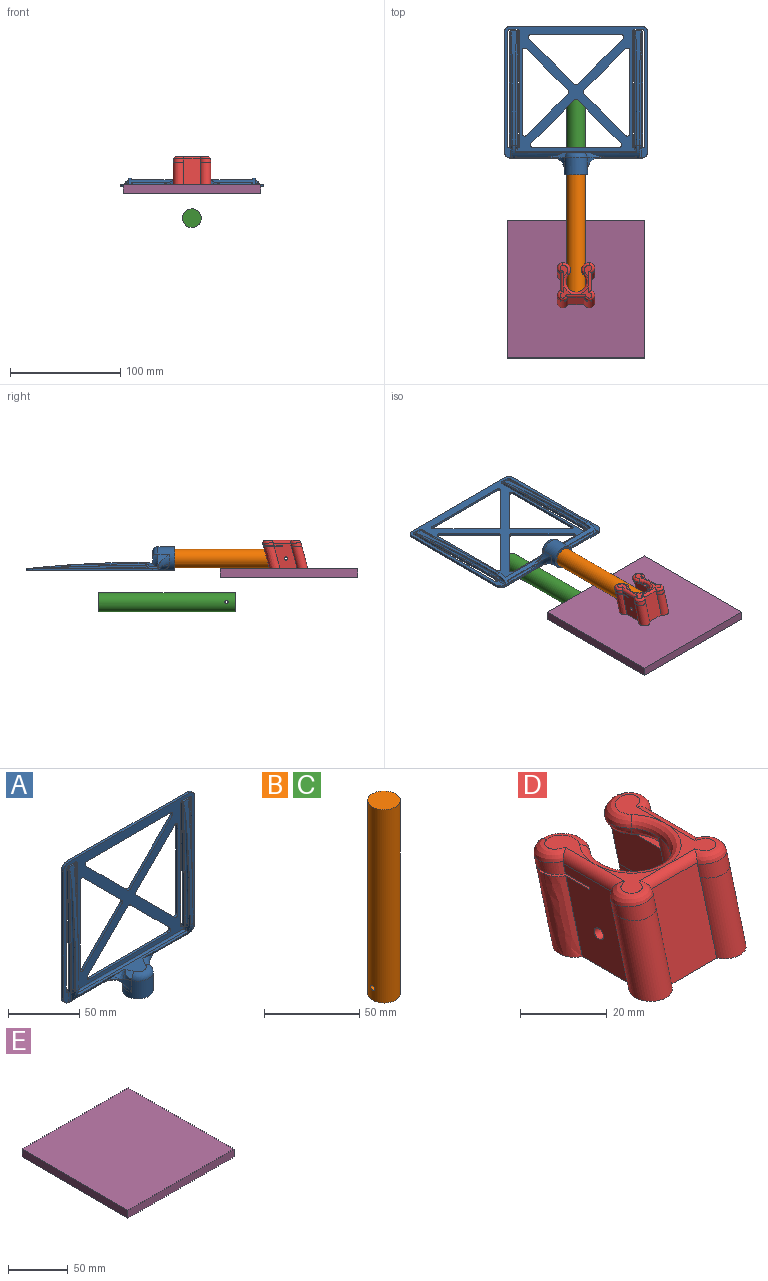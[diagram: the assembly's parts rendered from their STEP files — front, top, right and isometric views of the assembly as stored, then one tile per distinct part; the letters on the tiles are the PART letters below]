
ASSEMBLY  parts=5 mates=3
PART A: 120 faces, bbox 131.6x28.9x138.7 mm
  f0: plane 41.75x4.12mm, normal (0,0,-1), area 89.4mm2, adj f3,f11,f19,f53,f109,f115
  f1: plane 35.86x0.49mm, normal (0,0,-1), area 17.4mm2, adj f4,f9,f19,f113
  f2: cylinder r=15.3mm len=49.77mm, axis (-1,0,0), area 182.8mm2, adj f5,f7,f8,f14,f15,f17,f20,f101
  f3: plane 24.89x0.51mm, normal (0,-1,0), area 12.3mm2, adj f0,f4,f104,f109,f113
  f4: cylinder r=1.5mm len=34.86mm, axis (1,0,0), area 71.8mm2, adj f1,f3,f104,f113
  f5: plane 83.74x4mm, normal (-1,0,0), area 95.1mm2, adj f2,f20,f101,f102,f103
  f6: plane 83.74x4mm, normal (1,0,0), area 95.1mm2, adj f19,f21,f91,f92,f93
  f7: plane 80.18x4mm, normal (1,0,0), area 90.3mm2, adj f2,f17,f20,f94,f95,f96
  f8: plane 0.57x0.49mm, normal (1,0,0), area 0.1mm2, adj f2,f15,f106
  f9: plane 0.57x0.49mm, normal (-1,0,0), area 0.1mm2, adj f1,f19,f104
  f10: plane 80.18x4mm, normal (-1,0,0), area 90.3mm2, adj f17,f19,f21,f98,f99,f100
  f11: plane 131.62x121.62mm, normal (0,1,0), area 5467.3mm2, adj f0,f14,f24,f26,f36,f37,f38,f39
  f12: plane 6.61x0.05mm, normal (0,1,0), area 0.3mm2, adj f16,f27,f32,f35
  f13: plane 6x2mm, normal (0,0,1), area 12mm2, adj f18,f20,f29,f30
  f14: plane 41.75x4.12mm, normal (0,0,-1), area 89.4mm2, adj f2,f11,f54,f90,f110,f116
  f15: plane 35.86x0.49mm, normal (0,0,-1), area 17.4mm2, adj f2,f8,f105,f111
  f16: plane 6x2mm, normal (0,0,1), area 12mm2, adj f12,f21,f32,f35
  f17: plane 110x13.2mm, normal (0,0,1), area 400.8mm2, adj f2,f7,f10,f19,f97,f111,f112,f113
  f18: plane 6.61x0.05mm, normal (0,1,0), area 0.3mm2, adj f13,f22,f29,f30
  f19: cylinder r=15.3mm len=49.77mm, axis (-1,0,0), area 182.8mm2, adj f0,f1,f6,f9,f10,f17,f21,f92
  f20: cylinder r=981.3mm len=103.75mm, axis (-1,0,0), area 357.5mm2, adj f2,f5,f7,f13,f94,f102
  f21: cylinder r=981.3mm len=103.75mm, axis (-1,0,0), area 357.5mm2, adj f6,f10,f16,f19,f91,f99
  f22: cylinder r=2152.06mm len=103.7mm, axis (-1,0,0), area 829.3mm2, adj f18,f23,f28,f29,f30,f31
  f23: cylinder r=0.5mm len=8mm, axis (-1,0,0), area 6.3mm2, adj f22,f24,f28,f31
  f24: cylinder r=2mm len=9.5mm, axis (-1,0,0), area 25.7mm2, adj f11,f23,f28,f31,f59,f60
  f25: cylinder r=0.5mm len=8mm, axis (-1,0,0), area 6.3mm2, adj f26,f27,f33,f34
  f26: cylinder r=2mm len=9.5mm, axis (-1,0,0), area 25.7mm2, adj f11,f25,f33,f34,f47,f48
  f27: cylinder r=2152.06mm len=103.7mm, axis (-1,0,0), area 829.3mm2, adj f12,f25,f32,f33,f34,f35
  f28: plane 104.5x4.45mm, normal (-1,0,0), area 211mm2, adj f22,f23,f24,f29,f59,f83,f85
  f29: cylinder r=1mm len=2.05mm, axis (0,1,0), area 3.2mm2, adj f13,f18,f22,f28,f85
  f30: cylinder r=1mm len=2.05mm, axis (0,1,0), area 3.2mm2, adj f13,f18,f22,f31,f84
  f31: plane 104.5x4.45mm, normal (1,0,0), area 211mm2, adj f22,f23,f24,f30,f60,f82,f84
  f32: cylinder r=1mm len=2.05mm, axis (0,1,0), area 3.2mm2, adj f12,f16,f27,f33,f89
  f33: plane 104.5x4.45mm, normal (1,0,0), area 211mm2, adj f25,f26,f27,f32,f48,f87,f89
  f34: plane 104.5x4.45mm, normal (-1,0,0), area 211mm2, adj f25,f26,f27,f35,f47,f86,f88
  f35: cylinder r=1mm len=2.05mm, axis (0,1,0), area 3.2mm2, adj f12,f16,f27,f34,f88
  f36: cylinder r=2mm len=3.41mm, axis (0,1,0), area 9.4mm2, adj f11,f76,f80,f81
  f37: plane 104.5x2mm, normal (-1,0,0), area 209mm2, adj f11,f43,f48,f81
  f38: plane 109x2mm, normal (-1,0,0), area 218mm2, adj f11,f49,f54,f81
  f39: plane 104.5x2mm, normal (-1,0,0), area 209mm2, adj f11,f55,f60,f81
  f40: plane 39.51x39.51mm, normal (-0.71,0,-0.71), area 111.8mm2, adj f11,f61,f65,f81
  f41: cylinder r=2mm len=2.83mm, axis (0,1,0), area 6.3mm2, adj f11,f66,f70,f81
  f42: cylinder r=2mm len=3.41mm, axis (0,1,0), area 9.4mm2, adj f11,f71,f75,f81
  f43: cylinder r=2.5mm len=2.5mm, axis (0,1,0), area 7.9mm2, adj f11,f37,f44,f81
  f44: plane 6x2mm, normal (0,0,-1), area 12mm2, adj f11,f43,f45,f81
  f45: cylinder r=2.5mm len=2.5mm, axis (0,1,0), area 7.9mm2, adj f11,f44,f46,f81
  f46: plane 104.5x2mm, normal (1,0,0), area 209mm2, adj f11,f45,f47,f81
  f47: cylinder r=0.75mm len=3.79mm, axis (0,1,0), area 5.7mm2, adj f11,f26,f34,f46,f81,f86
  f48: cylinder r=0.75mm len=3.79mm, axis (0,1,0), area 5.7mm2, adj f11,f26,f33,f37,f81,f87
  f49: cylinder r=5.5mm len=5.5mm, axis (0,1,0), area 17.3mm2, adj f11,f38,f50,f81
  f50: plane 119x2mm, normal (0,0,1), area 238mm2, adj f11,f49,f51,f81
  f51: cylinder r=5.5mm len=5.5mm, axis (0,1,0), area 17.3mm2, adj f11,f50,f52,f81
  f52: plane 109x2mm, normal (1,0,0), area 218mm2, adj f11,f51,f53,f81
  f53: cylinder r=5.5mm len=5.5mm, axis (0,1,0), area 17.3mm2, adj f0,f11,f52,f81
  f54: cylinder r=5.5mm len=5.5mm, axis (0,1,0), area 17.3mm2, adj f11,f14,f38,f81
  f55: cylinder r=2.5mm len=2.5mm, axis (0,1,0), area 7.9mm2, adj f11,f39,f56,f81
  f56: plane 6x2mm, normal (0,0,-1), area 12mm2, adj f11,f55,f57,f81
  f57: cylinder r=2.5mm len=2.5mm, axis (0,1,0), area 7.9mm2, adj f11,f56,f58,f81
  f58: plane 104.5x2mm, normal (1,0,0), area 209mm2, adj f11,f57,f59,f81
  f59: cylinder r=0.75mm len=3.79mm, axis (0,1,0), area 5.7mm2, adj f11,f24,f28,f58,f81,f83
  f60: cylinder r=0.75mm len=3.79mm, axis (0,1,0), area 5.7mm2, adj f11,f24,f31,f39,f81,f82
  f61: cylinder r=2mm len=2.83mm, axis (0,1,0), area 6.3mm2, adj f11,f40,f62,f81
  f62: plane 39.51x39.51mm, normal (0.71,0,-0.71), area 111.8mm2, adj f11,f61,f63,f81
  f63: cylinder r=2mm len=3.41mm, axis (0,1,0), area 9.4mm2, adj f11,f62,f64,f81
  f64: plane 79.03x2mm, normal (0,0,1), area 158.1mm2, adj f11,f63,f65,f81
  f65: cylinder r=2mm len=3.41mm, axis (0,1,0), area 9.4mm2, adj f11,f40,f64,f81
  f66: plane 41.51x41.51mm, normal (-0.71,0,0.71), area 117.4mm2, adj f11,f41,f67,f81
  f67: cylinder r=2mm len=3.41mm, axis (0,1,0), area 9.4mm2, adj f11,f66,f68,f81
  f68: plane 83.03x2mm, normal (0,0,-1), area 166.1mm2, adj f11,f67,f69,f81
  f69: cylinder r=2mm len=3.41mm, axis (0,1,0), area 9.4mm2, adj f11,f68,f70,f81
  f70: plane 41.51x41.51mm, normal (0.71,0,0.71), area 117.4mm2, adj f11,f41,f69,f81
  f71: plane 38.01x38.01mm, normal (-0.71,0,0.71), area 107.5mm2, adj f11,f42,f72,f81
  f72: cylinder r=2mm len=2.83mm, axis (0,1,0), area 6.3mm2, adj f11,f71,f73,f81
  f73: plane 38.01x38.01mm, normal (-0.71,0,-0.71), area 107.5mm2, adj f11,f72,f74,f81
  f74: cylinder r=2mm len=3.41mm, axis (0,1,0), area 9.4mm2, adj f11,f73,f75,f81
  f75: plane 76.03x2mm, normal (1,0,0), area 152.1mm2, adj f11,f42,f74,f81
  f76: plane 38.01x38.01mm, normal (0.71,0,-0.71), area 107.5mm2, adj f11,f36,f77,f81
  f77: cylinder r=2mm len=2.83mm, axis (0,1,0), area 6.3mm2, adj f11,f76,f78,f81
  f78: plane 38.01x38.01mm, normal (0.71,0,0.71), area 107.5mm2, adj f11,f77,f79,f81
  f79: cylinder r=2mm len=3.41mm, axis (0,1,0), area 9.4mm2, adj f11,f78,f80,f81
  f80: plane 76.03x2mm, normal (-1,0,0), area 152.1mm2, adj f11,f36,f79,f81
  f81: plane 130x120mm, normal (0,-1,0), area 4660.8mm2, adj f36,f37,f38,f39,f40,f41,f42,f43
  f82: cylinder r=2.5mm len=2.5mm, axis (-1,0,0), area 4.7mm2, adj f31,f60,f81,f84,f95
  f83: cylinder r=2.5mm len=2.5mm, axis (-1,0,0), area 4.7mm2, adj f28,f59,f81,f85,f103
  f84: cylinder r=2154.06mm len=103.75mm, axis (-1,0,0), area 103.3mm2, adj f30,f31,f82,f94
  f85: cylinder r=2154.06mm len=103.75mm, axis (-1,0,0), area 103.3mm2, adj f28,f29,f83,f102
  f86: cylinder r=2.5mm len=2.5mm, axis (-1,0,0), area 4.7mm2, adj f34,f47,f81,f88,f100
  f87: cylinder r=2.5mm len=2.5mm, axis (-1,0,0), area 4.7mm2, adj f33,f48,f81,f89,f93
  f88: cylinder r=2154.06mm len=103.75mm, axis (-1,0,0), area 103.3mm2, adj f34,f35,f86,f99
  f89: cylinder r=2154.06mm len=103.75mm, axis (-1,0,0), area 103.3mm2, adj f32,f33,f87,f91
  f90: plane 24.88x0.5mm, normal (0,-1,0), area 12.3mm2, adj f14,f105,f106,f110,f111
  f91: torus R=2155.56mm, axis (-1,0,0), area 208.8mm2, adj f6,f21,f89,f93
  f92: cylinder r=1.5mm len=9.25mm, axis (0,0,1), area 18.7mm2, adj f6,f19,f81,f93
  f93: torus R=4mm, axis (-1,0,0), area 9.8mm2, adj f6,f87,f91,f92
  f94: torus R=2155.56mm, axis (-1,0,0), area 208.8mm2, adj f7,f20,f84,f95
  f95: torus R=4mm, axis (-1,0,0), area 9.8mm2, adj f7,f82,f94,f96
  f96: cylinder r=1.5mm len=4.25mm, axis (0,0,1), area 6.8mm2, adj f7,f81,f95,f97
  f97: cylinder r=1.5mm len=110mm, axis (-1,0,0), area 255.6mm2, adj f17,f81,f96,f98
  f98: cylinder r=1.5mm len=4.25mm, axis (0,0,-1), area 6.8mm2, adj f10,f81,f97,f100
  f99: torus R=2155.56mm, axis (1,0,0), area 208.8mm2, adj f10,f21,f88,f100
  f100: torus R=4mm, axis (1,0,0), area 9.8mm2, adj f10,f86,f98,f99
  f101: cylinder r=1.5mm len=9.25mm, axis (0,0,-1), area 18.7mm2, adj f2,f5,f81,f103
  f102: torus R=2155.56mm, axis (1,0,0), area 208.8mm2, adj f5,f20,f85,f103
  f103: torus R=4mm, axis (1,0,0), area 9.8mm2, adj f5,f83,f101,f102
  f104: cylinder r=1.5mm len=2mm, axis (0,0,-1), area 2.3mm2, adj f3,f4,f9,f19
  f105: cylinder r=1.5mm len=34.86mm, axis (1,0,0), area 71.8mm2, adj f15,f90,f106,f111
  f106: cylinder r=1.5mm len=2mm, axis (0,0,1), area 2.3mm2, adj f2,f8,f90,f105
  f107: cylinder r=10.75mm len=21.5mm, axis (0,0,1), area 710.4mm2, adj f108,f109,f110,f112,f114,f115,f116,f117
  f108: plane 21.5x21.5mm, normal (0,0,-1), area 122.5mm2, adj f107,f119
  f109: cylinder r=20mm len=18.61mm, axis (0,0,1), area 54.9mm2, adj f0,f3,f107,f113,f115
  f110: cylinder r=20mm len=18.61mm, axis (0,0,1), area 54.9mm2, adj f14,f90,f107,f111,f116
  f111: torus R=24.8mm, axis (0,0,1), area 99.6mm2, adj f2,f15,f17,f90,f105,f110,f112
  f112: torus R=5.95mm, axis (0,0,1), area 162.5mm2, adj f17,f107,f111,f113
  f113: torus R=24.8mm, axis (0,0,1), area 99.3mm2, adj f1,f3,f4,f17,f19,f109,f112
  f114: bspline ~18.55x10.67mm, area 0mm2, adj f11,f107,f115
  f115: torus R=20.75mm, axis (0,0,1), area 119mm2, adj f0,f107,f109,f114
  f116: torus R=20.75mm, axis (0,0,1), area 119mm2, adj f14,f107,f110,f117
  f117: bspline ~18.55x10.67mm, area 0mm2, adj f11,f107,f116
  f118: plane 17.5x17.5mm, normal (0,0,-1), area 240.5mm2, adj f119
  f119: cylinder r=8.75mm len=17.5mm, axis (0,0,1), area 824.7mm2, adj f108,f118
PART B: 4 faces, bbox 17x17x124 mm
  f0: cylinder r=8.5mm len=124mm, axis (0,0,-1), area 6608.3mm2, adj f1,f2,f3
  f1: plane 17x17mm, normal (0,0,1), area 227mm2, adj f0
  f2: plane 17x17mm, normal (0,0,-1), area 227mm2, adj f0
  f3: cylinder r=1.5mm len=17mm, axis (-1,0,0), area 159mm2, adj f0
PART C: same geometry as B
PART D: 61 faces, bbox 44.2x43.7x35.1 mm
  f0: cylinder r=9mm len=8.67mm, axis (0,-1,0), area 40.5mm2, adj f1,f58,f59,f60
  f1: cylinder r=1.5mm len=5.08mm, axis (-1,0,0), area 47.3mm2, adj f0,f2,f54,f55,f56,f57,f58,f60
  f2: plane 23.12x21.89mm, normal (-1,0,0), area 351.3mm2, adj f1,f3,f40,f41,f47,f48,f49,f50
  f3: bspline ~10.43x9.51mm, area 56.1mm2, adj f2,f4,f40,f53
  f4: plane 23.75x14.97mm, normal (0,-0.97,0.26), area 366.3mm2, adj f3,f5,f37,f38,f39,f40,f41,f53
  f5: bspline ~10.43x9.51mm, area 56.1mm2, adj f4,f6,f37,f39
  f6: plane 23.12x21.89mm, normal (1,0,0), area 351.3mm2, adj f5,f7,f16,f30,f31,f33,f35,f36
  f7: cylinder r=1.5mm len=5.08mm, axis (-1,0,0), area 47.3mm2, adj f6,f8,f9,f11,f12,f54,f55,f56
  f8: cylinder r=9mm len=8.67mm, axis (0,-1,0), area 40.5mm2, adj f7,f9,f12,f59
  f9: bspline ~9.38x7.74mm, area 23.9mm2, adj f7,f8,f10,f54
  f10: bspline ~6.06x2.48mm, area 14.1mm2, adj f9,f54,f58,f59
  f11: plane 18.98x11mm, normal (-1,0,0), area 179.2mm2, adj f7,f31,f33,f54,f56
  f12: plane 8.37x8.27mm, normal (-1,0,0), area 45.8mm2, adj f7,f8,f13,f55,f59
  f13: bspline ~18x14.64mm, area 58.5mm2, adj f12,f14,f41,f55,f59,f60
  f14: bspline ~26.21x19.06mm, area 0mm2, adj f13,f15
  f15: bspline ~12.4x2.34mm, area 0mm2, adj f14,f59
  f16: plane 15.53x9.51mm, normal (0,0,-1), area 86mm2, adj f6,f17,f29,f30,f36
  f17: bspline ~16.84x11.31mm, area 57.8mm2, adj f16,f18,f29,f36
  f18: bspline ~11.77x8.23mm, area 59.2mm2, adj f17,f19,f27,f28
  f19: bspline ~23x20.69mm, area 193mm2, adj f18,f20,f21,f23,f25,f26,f28,f29
  f20: plane 14.84x14.5mm, normal (0,0,1), area 46.3mm2, adj f19,f38,f52,f53
  f21: plane 14.85x7mm, normal (0,0,1), area 42.4mm2, adj f19,f22,f23,f52
  f22: bspline ~10.96x6.13mm, area 44.1mm2, adj f21,f23,f51,f52
  f23: bspline ~11.8x8.02mm, area 59.2mm2, adj f19,f21,f22,f24
  f24: bspline ~16.84x11.27mm, area 57.8mm2, adj f23,f25,f50,f51
  f25: bspline ~8.68x4.84mm, area 33mm2, adj f19,f24,f49,f50
  f26: plane 14.84x14.5mm, normal (0,0,1), area 46.3mm2, adj f19,f35,f38,f39
  f27: bspline ~10.96x6.13mm, area 44.1mm2, adj f18,f28,f35,f36
  f28: plane 14.86x7mm, normal (0,0,1), area 42.4mm2, adj f18,f19,f27,f35
  f29: bspline ~8.68x4.84mm, area 33mm2, adj f16,f17,f19,f30
  f30: plane 5x3mm, normal (0,0.97,-0.26), area 4mm2, adj f6,f16,f29,f31,f54
  f31: plane 17.98x8.56mm, normal (0,0,1), area 93.1mm2, adj f6,f11,f30,f32,f33
  f32: bspline ~20.1x13.39mm, area 257.5mm2, adj f31,f41
  f33: bspline ~20.1x16.23mm, area 362.6mm2, adj f6,f11,f31,f34,f41,f56
  f34: plane 14.9x4.05mm, normal (0,0.97,-0.26), area 19.6mm2, adj f33,f41,f47,f56
  f35: cylinder r=2.5mm len=19.12mm, axis (0,-1,0), area 67.3mm2, adj f6,f26,f27,f28,f36,f39
  f36: bspline ~11.06x6.94mm, area 28.8mm2, adj f6,f16,f17,f27,f35
  f37: bspline ~20.1x14.94mm, area 396.7mm2, adj f4,f5,f6,f41
  f38: cylinder r=2.5mm len=18.07mm, axis (-1,0,0), area 54mm2, adj f4,f20,f26,f39,f53
  f39: bspline ~10.67x10.34mm, area 62.5mm2, adj f4,f5,f6,f26,f35,f38
  f40: bspline ~20.1x14.94mm, area 396.7mm2, adj f2,f3,f4,f41
  f41: plane 35.4x34.56mm, normal (0,0,-1), area 702.7mm2, adj f2,f4,f6,f13,f32,f33,f34,f37
  f42: bspline ~20.1x13.39mm, area 257.5mm2, adj f41,f48
  f43: bspline ~20.1x13.39mm, area 257.5mm2, adj f41,f44
  f44: plane 4.56x4.56mm, normal (0,0,-1), area 12.6mm2, adj f43
  f45: bspline ~20.1x13.39mm, area 257.5mm2, adj f41,f46
  f46: plane 4.56x4.56mm, normal (0,0,-1), area 12.6mm2, adj f45
  f47: bspline ~20.1x16.23mm, area 362.3mm2, adj f2,f34,f41,f48,f56,f57
  f48: plane 17.98x8.56mm, normal (0,0,1), area 93.1mm2, adj f2,f42,f47,f49,f57
  f49: plane 5x3mm, normal (0,0.97,-0.26), area 4mm2, adj f2,f25,f48,f50,f54
  f50: plane 15.53x9.51mm, normal (0,0,-1), area 86mm2, adj f2,f24,f25,f49,f51
  f51: bspline ~11.06x6.94mm, area 28.8mm2, adj f2,f22,f24,f50,f52
  f52: cylinder r=2.5mm len=19.12mm, axis (0,1,0), area 67.3mm2, adj f2,f20,f21,f22,f51,f53
  f53: bspline ~10.67x10.34mm, area 62.5mm2, adj f2,f3,f4,f20,f38,f52
  f54: cylinder r=9mm len=18mm, axis (0,0.26,0.97), area 193.9mm2, adj f1,f7,f9,f10,f11,f19,f30,f49
  f55: cylinder r=9mm len=18mm, axis (0,-0.26,-0.97), area 93.7mm2, adj f1,f7,f12,f13,f41,f56,f60
  f56: cylinder r=9mm len=18mm, axis (0,-1,0), area 250.9mm2, adj f1,f7,f11,f33,f34,f47,f55,f57
  f57: plane 18.98x11mm, normal (1,0,0), area 179.2mm2, adj f1,f47,f48,f54,f56
  f58: bspline ~9.38x7.74mm, area 23.9mm2, adj f0,f1,f10,f54
  f59: bspline ~18x16.87mm, area 278.7mm2, adj f0,f8,f10,f12,f13,f15,f60
  f60: plane 8.37x8.27mm, normal (1,0,0), area 45.8mm2, adj f0,f1,f13,f55,f59
PART E: 6 faces, bbox 125x125x8 mm
  f0: plane 125x8mm, normal (1,0,0), area 1000mm2, adj f1,f3,f4,f5
  f1: plane 125x8mm, normal (0,-1,0), area 1000mm2, adj f0,f2,f4,f5
  f2: plane 125x8mm, normal (-1,0,0), area 1000mm2, adj f1,f3,f4,f5
  f3: plane 125x8mm, normal (0,1,0), area 1000mm2, adj f0,f2,f4,f5
  f4: plane 125x125mm, normal (0,0,-1), area 15625mm2, adj f0,f1,f2,f3
  f5: plane 125x125mm, normal (0,0,1), area 15625mm2, adj f0,f1,f2,f3
PLACE A rot(axis=(-1,0,0),90deg) t=(0,178.93,6.35)mm
PLACE B rot(axis=(-1,0,0),90deg) t=(0,-5.07,17.1)mm
PLACE C rot(axis=(0,0.71,0.71),180deg) t=(0,48.9,-22.53)mm
PLACE D t=(0,2.93,17.1)mm
PLACE E rot(axis=(0,1,0),180deg) t=(0,0,0)mm
MATE fastened D.f41 <-> E.f4  axis (0,0,-1) through (0,0,8)mm
MATE fastened B.f0 <-> A.f107  axis (0,1,0) through (0,118.93,17.1)mm
MATE cylindrical D.f1 <-> B.f3  axis (-1,0,0) through (14,2.93,17.1)mm
